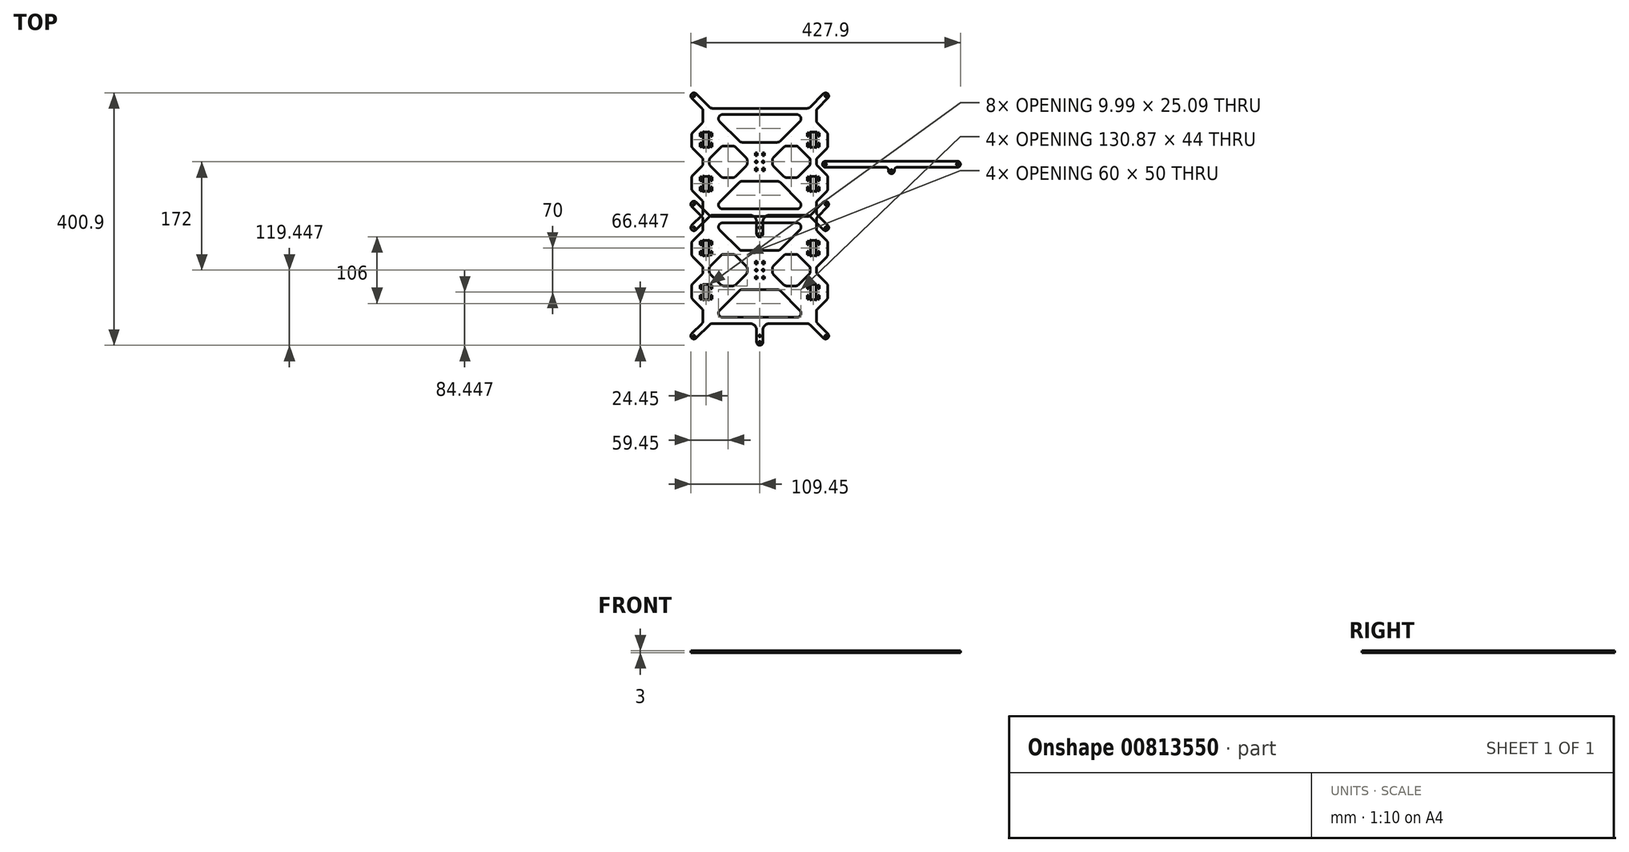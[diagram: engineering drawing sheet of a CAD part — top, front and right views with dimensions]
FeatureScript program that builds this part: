
annotation { "Feature Type Name" : "Feature", "Feature Type Description" : "" }
export const myFeature = defineFeature(function(context is Context, id is Id, definition is map)
    precondition{}
    {
        {
            var Q0;
            Q0=qCreatedBy(makeId("Top.planeOp"),FACE);
            var sketch = newSketch(context, id + "F0", { "sketchPlane" : qUnion([Q0])});
            skCircle(sketch, "E0", {"center": v(5.5, 8.85) * mm, "radius": 1.6 * mm});
            skCircle(sketch, "E1", {"center": v(-104.5, -95.65) * mm, "radius": 1.25 * mm});
            skCircle(sketch, "E2", {"center": v(-104.5, 113.35) * mm, "radius": 1.25 * mm});
            skCircle(sketch, "E3", {"center": v(0, -105.65) * mm, "radius": 1.6 * mm});
            skArc(sketch, "E4", {"start": v(-91.76, 70.09) * mm, "mid": v(-90.46, 72.04) * mm, "end": v(-90, 74.33) * mm});
            skLineSegment(sketch, "E5", {"start": v(-91.76, 70.09) * mm, "end": v(-106.24, 55.6) * mm});
            skArc(sketch, "E6", {"start": v(-106.24, 55.6) * mm, "mid": v(-107.54, 53.66) * mm, "end": v(-108, 51.36) * mm});
            skLineSegment(sketch, "E7", {"start": v(-108, 51.36) * mm, "end": v(-108, 34.33) * mm});
            skArc(sketch, "E8", {"start": v(-108, 34.33) * mm, "mid": v(-107.54, 32.04) * mm, "end": v(-106.24, 30.09) * mm});
            skLineSegment(sketch, "E9", {"start": v(-106.24, 30.09) * mm, "end": v(-91.76, 15.6) * mm});
            skArc(sketch, "E10", {"start": v(-90, 11.36) * mm, "mid": v(-90.46, 13.66) * mm, "end": v(-91.76, 15.6) * mm});
            skLineSegment(sketch, "E11", {"start": v(-90, 11.36) * mm, "end": v(-90, 6.33) * mm});
            skArc(sketch, "E12", {"start": v(-91.76, 2.09) * mm, "mid": v(-90.46, 4.04) * mm, "end": v(-90, 6.33) * mm});
            skLineSegment(sketch, "E13", {"start": v(-91.76, 2.09) * mm, "end": v(-106.24, -12.4) * mm});
            skArc(sketch, "E14", {"start": v(-106.24, -12.4) * mm, "mid": v(-107.54, -14.34) * mm, "end": v(-108, -16.64) * mm});
            skLineSegment(sketch, "E15", {"start": v(-108, -16.64) * mm, "end": v(-108, -33.67) * mm});
            skArc(sketch, "E16", {"start": v(-108, -33.67) * mm, "mid": v(-107.54, -35.96) * mm, "end": v(-106.24, -37.91) * mm});
            skLineSegment(sketch, "E17", {"start": v(-106.24, -37.91) * mm, "end": v(-91.76, -52.4) * mm});
            skArc(sketch, "E18", {"start": v(-90, -56.64) * mm, "mid": v(-90.46, -54.34) * mm, "end": v(-91.76, -52.4) * mm});
            skLineSegment(sketch, "E19", {"start": v(-90, -56.64) * mm, "end": v(-90, -71.67) * mm});
            skArc(sketch, "E20", {"start": v(-91.76, -75.91) * mm, "mid": v(-90.46, -73.96) * mm, "end": v(-90, -71.67) * mm});
            skLineSegment(sketch, "E21", {"start": v(-91.76, -75.91) * mm, "end": v(-108, -92.15) * mm});
            skArc(sketch, "E22", {"start": v(-108, -92.15) * mm, "mid": v(-108, -99.15) * mm, "end": v(-101, -99.15) * mm});
            skLineSegment(sketch, "E23", {"start": v(-101, -99.15) * mm, "end": v(-79.76, -77.91) * mm});
            skArc(sketch, "E24", {"start": v(-75.51, -76.15) * mm, "mid": v(-77.81, -76.6) * mm, "end": v(-79.76, -77.91) * mm});
            skLineSegment(sketch, "E25", {"start": v(-75.51, -76.15) * mm, "end": v(-14.95, -76.15) * mm});
            skArc(sketch, "E26", {"start": v(-4.95, -86.15) * mm, "mid": v(-7.88, -79.08) * mm, "end": v(-14.95, -76.15) * mm});
            skLineSegment(sketch, "E27", {"start": v(-4.95, -86.15) * mm, "end": v(-4.95, -105.65) * mm});
            skArc(sketch, "E28", {"start": v(-4.95, -105.65) * mm, "mid": v(0, -110.6) * mm, "end": v(4.95, -105.65) * mm});
            skLineSegment(sketch, "E29", {"start": v(4.95, -105.65) * mm, "end": v(4.95, -86.15) * mm});
            skArc(sketch, "E30", {"start": v(14.95, -76.15) * mm, "mid": v(7.88, -79.08) * mm, "end": v(4.95, -86.15) * mm});
            skLineSegment(sketch, "E31", {"start": v(14.95, -76.15) * mm, "end": v(75.51, -76.15) * mm});
            skArc(sketch, "E32", {"start": v(79.76, -77.91) * mm, "mid": v(77.81, -76.6) * mm, "end": v(75.51, -76.15) * mm});
            skLineSegment(sketch, "E33", {"start": v(79.76, -77.91) * mm, "end": v(101, -99.15) * mm});
            skArc(sketch, "E34", {"start": v(101, -99.15) * mm, "mid": v(108, -99.15) * mm, "end": v(108, -92.15) * mm});
            skLineSegment(sketch, "E35", {"start": v(108, -92.15) * mm, "end": v(91.76, -75.91) * mm});
            skArc(sketch, "E36", {"start": v(90, -71.67) * mm, "mid": v(90.46, -73.96) * mm, "end": v(91.76, -75.91) * mm});
            skLineSegment(sketch, "E37", {"start": v(90, -71.67) * mm, "end": v(90, -56.64) * mm});
            skArc(sketch, "E38", {"start": v(91.76, -52.4) * mm, "mid": v(90.46, -54.34) * mm, "end": v(90, -56.64) * mm});
            skLineSegment(sketch, "E39", {"start": v(91.76, -52.4) * mm, "end": v(106.24, -37.91) * mm});
            skArc(sketch, "E40", {"start": v(106.24, -37.91) * mm, "mid": v(107.54, -35.96) * mm, "end": v(108, -33.67) * mm});
            skLineSegment(sketch, "E41", {"start": v(108, -33.67) * mm, "end": v(108, -16.64) * mm});
            skArc(sketch, "E42", {"start": v(108, -16.64) * mm, "mid": v(107.54, -14.34) * mm, "end": v(106.24, -12.4) * mm});
            skLineSegment(sketch, "E43", {"start": v(106.24, -12.4) * mm, "end": v(91.76, 2.09) * mm});
            skArc(sketch, "E44", {"start": v(90, 6.33) * mm, "mid": v(90.46, 4.04) * mm, "end": v(91.76, 2.09) * mm});
            skLineSegment(sketch, "E45", {"start": v(90, 6.33) * mm, "end": v(90, 11.36) * mm});
            skArc(sketch, "E46", {"start": v(91.76, 15.6) * mm, "mid": v(90.46, 13.66) * mm, "end": v(90, 11.36) * mm});
            skLineSegment(sketch, "E47", {"start": v(91.76, 15.6) * mm, "end": v(106.24, 30.09) * mm});
            skArc(sketch, "E48", {"start": v(106.24, 30.09) * mm, "mid": v(107.54, 32.04) * mm, "end": v(108, 34.33) * mm});
            skLineSegment(sketch, "E49", {"start": v(108, 34.33) * mm, "end": v(108, 51.36) * mm});
            skArc(sketch, "E50", {"start": v(108, 51.36) * mm, "mid": v(107.54, 53.66) * mm, "end": v(106.24, 55.6) * mm});
            skLineSegment(sketch, "E51", {"start": v(106.24, 55.6) * mm, "end": v(91.76, 70.09) * mm});
            skArc(sketch, "E52", {"start": v(90, 74.33) * mm, "mid": v(90.46, 72.04) * mm, "end": v(91.76, 70.09) * mm});
            skLineSegment(sketch, "E53", {"start": v(90, 74.33) * mm, "end": v(90, 89.36) * mm});
            skArc(sketch, "E54", {"start": v(91.76, 93.6) * mm, "mid": v(90.46, 91.66) * mm, "end": v(90, 89.36) * mm});
            skLineSegment(sketch, "E55", {"start": v(91.76, 93.6) * mm, "end": v(108, 109.85) * mm});
            skArc(sketch, "E56", {"start": v(108, 109.85) * mm, "mid": v(108, 116.85) * mm, "end": v(101, 116.85) * mm});
            skLineSegment(sketch, "E57", {"start": v(101, 116.85) * mm, "end": v(79.76, 95.6) * mm});
            skArc(sketch, "E58", {"start": v(75.51, 93.85) * mm, "mid": v(77.81, 94.3) * mm, "end": v(79.76, 95.6) * mm});
            skLineSegment(sketch, "E59", {"start": v(75.51, 93.85) * mm, "end": v(-75.51, 93.85) * mm});
            skArc(sketch, "E60", {"start": v(-79.76, 95.6) * mm, "mid": v(-77.81, 94.3) * mm, "end": v(-75.51, 93.85) * mm});
            skLineSegment(sketch, "E61", {"start": v(-79.76, 95.6) * mm, "end": v(-101, 116.85) * mm});
            skArc(sketch, "E62", {"start": v(-101, 116.85) * mm, "mid": v(-108, 116.85) * mm, "end": v(-108, 109.85) * mm});
            skLineSegment(sketch, "E63", {"start": v(-108, 109.85) * mm, "end": v(-91.76, 93.6) * mm});
            skArc(sketch, "E64", {"start": v(-90, 89.36) * mm, "mid": v(-90.46, 91.66) * mm, "end": v(-91.76, 93.6) * mm});
            skLineSegment(sketch, "E65", {"start": v(-90, 89.36) * mm, "end": v(-90, 74.33) * mm});
            skLineSegment(sketch, "E66", {"start": v(89.5, -37.34) * mm, "end": v(89.5, -14.97) * mm});
            skArc(sketch, "E67", {"start": v(89.5, -37.34) * mm, "mid": v(89.57, -37.59) * mm, "end": v(89.75, -37.77) * mm});
            skArc(sketch, "E68", {"start": v(89.07, -38.45) * mm, "mid": v(89.85, -38.56) * mm, "end": v(89.75, -37.77) * mm});
            skArc(sketch, "E69", {"start": v(89.07, -38.45) * mm, "mid": v(88.88, -38.27) * mm, "end": v(88.63, -38.2) * mm});
            skLineSegment(sketch, "E70", {"start": v(81.37, -38.2) * mm, "end": v(88.63, -38.2) * mm});
            skArc(sketch, "E71", {"start": v(81.37, -38.2) * mm, "mid": v(81.12, -38.27) * mm, "end": v(80.93, -38.45) * mm});
            skArc(sketch, "E72", {"start": v(80.25, -37.77) * mm, "mid": v(80.15, -38.56) * mm, "end": v(80.93, -38.45) * mm});
            skArc(sketch, "E73", {"start": v(80.25, -37.77) * mm, "mid": v(80.43, -37.59) * mm, "end": v(80.5, -37.34) * mm});
            skLineSegment(sketch, "E74", {"start": v(80.5, -14.97) * mm, "end": v(80.5, -37.34) * mm});
            skArc(sketch, "E75", {"start": v(80.5, -14.97) * mm, "mid": v(80.43, -14.72) * mm, "end": v(80.25, -14.54) * mm});
            skArc(sketch, "E76", {"start": v(80.93, -13.85) * mm, "mid": v(80.15, -13.75) * mm, "end": v(80.25, -14.54) * mm});
            skArc(sketch, "E77", {"start": v(80.93, -13.85) * mm, "mid": v(81.12, -14.04) * mm, "end": v(81.37, -14.1) * mm});
            skLineSegment(sketch, "E78", {"start": v(88.63, -14.1) * mm, "end": v(81.37, -14.1) * mm});
            skArc(sketch, "E79", {"start": v(88.63, -14.1) * mm, "mid": v(88.88, -14.04) * mm, "end": v(89.07, -13.85) * mm});
            skArc(sketch, "E80", {"start": v(89.75, -14.54) * mm, "mid": v(89.85, -13.75) * mm, "end": v(89.07, -13.85) * mm});
            skArc(sketch, "E81", {"start": v(89.75, -14.54) * mm, "mid": v(89.57, -14.72) * mm, "end": v(89.5, -14.97) * mm});
            skLineSegment(sketch, "E82", {"start": v(32.73, 41.78) * mm, "end": v(63.53, 72.58) * mm});
            skArc(sketch, "E83", {"start": v(28.07, 39.85) * mm, "mid": v(30.6, 40.35) * mm, "end": v(32.73, 41.78) * mm});
            skLineSegment(sketch, "E84", {"start": v(-28.07, 39.85) * mm, "end": v(28.07, 39.85) * mm});
            skArc(sketch, "E85", {"start": v(-32.73, 41.78) * mm, "mid": v(-30.6, 40.35) * mm, "end": v(-28.07, 39.85) * mm});
            skLineSegment(sketch, "E86", {"start": v(-63.53, 72.58) * mm, "end": v(-32.73, 41.78) * mm});
            skArc(sketch, "E87", {"start": v(-58.87, 83.85) * mm, "mid": v(-64.96, 79.77) * mm, "end": v(-63.53, 72.58) * mm});
            skLineSegment(sketch, "E88", {"start": v(58.87, 83.85) * mm, "end": v(-58.87, 83.85) * mm});
            skArc(sketch, "E89", {"start": v(63.53, 72.58) * mm, "mid": v(64.96, 79.77) * mm, "end": v(58.87, 83.85) * mm});
            skLineSegment(sketch, "E90", {"start": v(21.76, 2.09) * mm, "end": v(38.24, -14.4) * mm});
            skArc(sketch, "E91", {"start": v(20, 6.33) * mm, "mid": v(20.46, 4.04) * mm, "end": v(21.76, 2.09) * mm});
            skLineSegment(sketch, "E92", {"start": v(20, 11.36) * mm, "end": v(20, 6.33) * mm});
            skArc(sketch, "E93", {"start": v(21.76, 15.6) * mm, "mid": v(20.46, 13.66) * mm, "end": v(20, 11.36) * mm});
            skLineSegment(sketch, "E94", {"start": v(38.24, 32.09) * mm, "end": v(21.76, 15.6) * mm});
            skArc(sketch, "E95", {"start": v(42.49, 33.85) * mm, "mid": v(40.19, 33.4) * mm, "end": v(38.24, 32.09) * mm});
            skLineSegment(sketch, "E96", {"start": v(57.51, 33.85) * mm, "end": v(42.49, 33.85) * mm});
            skArc(sketch, "E97", {"start": v(61.76, 32.09) * mm, "mid": v(59.81, 33.4) * mm, "end": v(57.51, 33.85) * mm});
            skLineSegment(sketch, "E98", {"start": v(78.24, 15.6) * mm, "end": v(61.76, 32.09) * mm});
            skArc(sketch, "E99", {"start": v(80, 11.36) * mm, "mid": v(79.54, 13.66) * mm, "end": v(78.24, 15.6) * mm});
            skLineSegment(sketch, "E100", {"start": v(80, 6.33) * mm, "end": v(80, 11.36) * mm});
            skArc(sketch, "E101", {"start": v(78.24, 2.09) * mm, "mid": v(79.54, 4.04) * mm, "end": v(80, 6.33) * mm});
            skLineSegment(sketch, "E102", {"start": v(61.76, -14.4) * mm, "end": v(78.24, 2.09) * mm});
            skArc(sketch, "E103", {"start": v(57.51, -16.15) * mm, "mid": v(59.81, -15.7) * mm, "end": v(61.76, -14.4) * mm});
            skLineSegment(sketch, "E104", {"start": v(42.49, -16.15) * mm, "end": v(57.51, -16.15) * mm});
            skArc(sketch, "E105", {"start": v(38.24, -14.4) * mm, "mid": v(40.19, -15.7) * mm, "end": v(42.49, -16.15) * mm});
            skLineSegment(sketch, "E106", {"start": v(63.53, -54.89) * mm, "end": v(32.73, -24.09) * mm});
            skArc(sketch, "E107", {"start": v(58.87, -66.15) * mm, "mid": v(64.96, -62.08) * mm, "end": v(63.53, -54.89) * mm});
            skLineSegment(sketch, "E108", {"start": v(-58.87, -66.15) * mm, "end": v(58.87, -66.15) * mm});
            skArc(sketch, "E109", {"start": v(-63.53, -54.89) * mm, "mid": v(-64.96, -62.08) * mm, "end": v(-58.87, -66.15) * mm});
            skLineSegment(sketch, "E110", {"start": v(-32.73, -24.09) * mm, "end": v(-63.53, -54.89) * mm});
            skArc(sketch, "E111", {"start": v(-28.07, -22.15) * mm, "mid": v(-30.6, -22.66) * mm, "end": v(-32.73, -24.09) * mm});
            skLineSegment(sketch, "E112", {"start": v(28.07, -22.15) * mm, "end": v(-28.07, -22.15) * mm});
            skArc(sketch, "E113", {"start": v(32.73, -24.09) * mm, "mid": v(30.6, -22.66) * mm, "end": v(28.07, -22.15) * mm});
            skLineSegment(sketch, "E114", {"start": v(-61.76, 32.09) * mm, "end": v(-78.24, 15.6) * mm});
            skArc(sketch, "E115", {"start": v(-57.51, 33.85) * mm, "mid": v(-59.81, 33.4) * mm, "end": v(-61.76, 32.09) * mm});
            skLineSegment(sketch, "E116", {"start": v(-42.49, 33.85) * mm, "end": v(-57.51, 33.85) * mm});
            skArc(sketch, "E117", {"start": v(-38.24, 32.09) * mm, "mid": v(-40.19, 33.4) * mm, "end": v(-42.49, 33.85) * mm});
            skLineSegment(sketch, "E118", {"start": v(-21.76, 15.6) * mm, "end": v(-38.24, 32.09) * mm});
            skArc(sketch, "E119", {"start": v(-20, 11.36) * mm, "mid": v(-20.46, 13.66) * mm, "end": v(-21.76, 15.6) * mm});
            skLineSegment(sketch, "E120", {"start": v(-20, 6.33) * mm, "end": v(-20, 11.36) * mm});
            skArc(sketch, "E121", {"start": v(-21.76, 2.09) * mm, "mid": v(-20.46, 4.04) * mm, "end": v(-20, 6.33) * mm});
            skLineSegment(sketch, "E122", {"start": v(-38.24, -14.4) * mm, "end": v(-21.76, 2.09) * mm});
            skArc(sketch, "E123", {"start": v(-42.49, -16.15) * mm, "mid": v(-40.19, -15.7) * mm, "end": v(-38.24, -14.4) * mm});
            skLineSegment(sketch, "E124", {"start": v(-57.51, -16.15) * mm, "end": v(-42.49, -16.15) * mm});
            skArc(sketch, "E125", {"start": v(-61.76, -14.4) * mm, "mid": v(-59.81, -15.7) * mm, "end": v(-57.51, -16.15) * mm});
            skLineSegment(sketch, "E126", {"start": v(-78.24, 2.09) * mm, "end": v(-61.76, -14.4) * mm});
            skArc(sketch, "E127", {"start": v(-80, 6.33) * mm, "mid": v(-79.54, 4.04) * mm, "end": v(-78.24, 2.09) * mm});
            skLineSegment(sketch, "E128", {"start": v(-80, 11.36) * mm, "end": v(-80, 6.33) * mm});
            skArc(sketch, "E129", {"start": v(-78.24, 15.6) * mm, "mid": v(-79.54, 13.66) * mm, "end": v(-80, 11.36) * mm});
            skLineSegment(sketch, "E130", {"start": v(-88.63, 31.8) * mm, "end": v(-81.37, 31.8) * mm});
            skArc(sketch, "E131", {"start": v(-88.63, 31.8) * mm, "mid": v(-88.88, 31.73) * mm, "end": v(-89.07, 31.55) * mm});
            skArc(sketch, "E132", {"start": v(-89.75, 32.23) * mm, "mid": v(-89.85, 31.44) * mm, "end": v(-89.07, 31.55) * mm});
            skArc(sketch, "E133", {"start": v(-89.75, 32.23) * mm, "mid": v(-89.57, 32.41) * mm, "end": v(-89.5, 32.66) * mm});
            skLineSegment(sketch, "E134", {"start": v(-89.5, 55.03) * mm, "end": v(-89.5, 32.66) * mm});
            skArc(sketch, "E135", {"start": v(-89.5, 55.03) * mm, "mid": v(-89.57, 55.28) * mm, "end": v(-89.75, 55.46) * mm});
            skArc(sketch, "E136", {"start": v(-89.07, 56.15) * mm, "mid": v(-89.85, 56.25) * mm, "end": v(-89.75, 55.46) * mm});
            skArc(sketch, "E137", {"start": v(-89.07, 56.15) * mm, "mid": v(-88.88, 55.96) * mm, "end": v(-88.63, 55.9) * mm});
            skLineSegment(sketch, "E138", {"start": v(-81.37, 55.9) * mm, "end": v(-88.63, 55.9) * mm});
            skArc(sketch, "E139", {"start": v(-81.37, 55.9) * mm, "mid": v(-81.12, 55.96) * mm, "end": v(-80.93, 56.15) * mm});
            skArc(sketch, "E140", {"start": v(-80.25, 55.46) * mm, "mid": v(-80.15, 56.25) * mm, "end": v(-80.93, 56.15) * mm});
            skArc(sketch, "E141", {"start": v(-80.25, 55.46) * mm, "mid": v(-80.43, 55.28) * mm, "end": v(-80.5, 55.03) * mm});
            skLineSegment(sketch, "E142", {"start": v(-80.5, 32.66) * mm, "end": v(-80.5, 55.03) * mm});
            skArc(sketch, "E143", {"start": v(-80.5, 32.66) * mm, "mid": v(-80.43, 32.41) * mm, "end": v(-80.25, 32.23) * mm});
            skArc(sketch, "E144", {"start": v(-80.93, 31.55) * mm, "mid": v(-80.15, 31.44) * mm, "end": v(-80.25, 32.23) * mm});
            skArc(sketch, "E145", {"start": v(-80.93, 31.55) * mm, "mid": v(-81.12, 31.73) * mm, "end": v(-81.37, 31.8) * mm});
            skLineSegment(sketch, "E146", {"start": v(-88.63, -38.2) * mm, "end": v(-81.37, -38.2) * mm});
            skArc(sketch, "E147", {"start": v(-88.63, -38.2) * mm, "mid": v(-88.88, -38.27) * mm, "end": v(-89.07, -38.45) * mm});
            skArc(sketch, "E148", {"start": v(-89.75, -37.77) * mm, "mid": v(-89.85, -38.56) * mm, "end": v(-89.07, -38.45) * mm});
            skArc(sketch, "E149", {"start": v(-89.75, -37.77) * mm, "mid": v(-89.57, -37.59) * mm, "end": v(-89.5, -37.34) * mm});
            skLineSegment(sketch, "E150", {"start": v(-89.5, -14.97) * mm, "end": v(-89.5, -37.34) * mm});
            skArc(sketch, "E151", {"start": v(-89.5, -14.97) * mm, "mid": v(-89.57, -14.72) * mm, "end": v(-89.75, -14.54) * mm});
            skArc(sketch, "E152", {"start": v(-89.07, -13.85) * mm, "mid": v(-89.85, -13.75) * mm, "end": v(-89.75, -14.54) * mm});
            skArc(sketch, "E153", {"start": v(-89.07, -13.85) * mm, "mid": v(-88.88, -14.04) * mm, "end": v(-88.63, -14.1) * mm});
            skLineSegment(sketch, "E154", {"start": v(-81.37, -14.1) * mm, "end": v(-88.63, -14.1) * mm});
            skArc(sketch, "E155", {"start": v(-81.37, -14.1) * mm, "mid": v(-81.12, -14.04) * mm, "end": v(-80.93, -13.85) * mm});
            skArc(sketch, "E156", {"start": v(-80.25, -14.54) * mm, "mid": v(-80.15, -13.75) * mm, "end": v(-80.93, -13.85) * mm});
            skArc(sketch, "E157", {"start": v(-80.25, -14.54) * mm, "mid": v(-80.43, -14.72) * mm, "end": v(-80.5, -14.97) * mm});
            skLineSegment(sketch, "E158", {"start": v(-80.5, -37.34) * mm, "end": v(-80.5, -14.97) * mm});
            skArc(sketch, "E159", {"start": v(-80.5, -37.34) * mm, "mid": v(-80.43, -37.59) * mm, "end": v(-80.25, -37.77) * mm});
            skArc(sketch, "E160", {"start": v(-80.93, -38.45) * mm, "mid": v(-80.15, -38.56) * mm, "end": v(-80.25, -37.77) * mm});
            skArc(sketch, "E161", {"start": v(-80.93, -38.45) * mm, "mid": v(-81.12, -38.27) * mm, "end": v(-81.37, -38.2) * mm});
            skLineSegment(sketch, "E162", {"start": v(89.5, 32.66) * mm, "end": v(89.5, 55.03) * mm});
            skArc(sketch, "E163", {"start": v(89.5, 32.66) * mm, "mid": v(89.57, 32.41) * mm, "end": v(89.75, 32.23) * mm});
            skArc(sketch, "E164", {"start": v(89.07, 31.55) * mm, "mid": v(89.85, 31.44) * mm, "end": v(89.75, 32.23) * mm});
            skArc(sketch, "E165", {"start": v(89.07, 31.55) * mm, "mid": v(88.88, 31.73) * mm, "end": v(88.63, 31.8) * mm});
            skLineSegment(sketch, "E166", {"start": v(81.37, 31.8) * mm, "end": v(88.63, 31.8) * mm});
            skArc(sketch, "E167", {"start": v(81.37, 31.8) * mm, "mid": v(81.12, 31.73) * mm, "end": v(80.93, 31.55) * mm});
            skArc(sketch, "E168", {"start": v(80.25, 32.23) * mm, "mid": v(80.15, 31.44) * mm, "end": v(80.93, 31.55) * mm});
            skArc(sketch, "E169", {"start": v(80.25, 32.23) * mm, "mid": v(80.43, 32.41) * mm, "end": v(80.5, 32.66) * mm});
            skLineSegment(sketch, "E170", {"start": v(80.5, 55.03) * mm, "end": v(80.5, 32.66) * mm});
            skArc(sketch, "E171", {"start": v(80.5, 55.03) * mm, "mid": v(80.43, 55.28) * mm, "end": v(80.25, 55.46) * mm});
            skArc(sketch, "E172", {"start": v(80.93, 56.15) * mm, "mid": v(80.15, 56.25) * mm, "end": v(80.25, 55.46) * mm});
            skArc(sketch, "E173", {"start": v(80.93, 56.15) * mm, "mid": v(81.12, 55.96) * mm, "end": v(81.37, 55.9) * mm});
            skLineSegment(sketch, "E174", {"start": v(88.63, 55.9) * mm, "end": v(81.37, 55.9) * mm});
            skArc(sketch, "E175", {"start": v(88.63, 55.9) * mm, "mid": v(88.88, 55.96) * mm, "end": v(89.07, 56.15) * mm});
            skArc(sketch, "E176", {"start": v(89.75, 55.46) * mm, "mid": v(89.85, 56.25) * mm, "end": v(89.07, 56.15) * mm});
            skArc(sketch, "E177", {"start": v(89.75, 55.46) * mm, "mid": v(89.57, 55.28) * mm, "end": v(89.5, 55.03) * mm});
            skCircle(sketch, "E178", {"center": v(0, -95.65) * mm, "radius": 1.6 * mm});
            skCircle(sketch, "E179", {"center": v(104.5, 113.35) * mm, "radius": 1.25 * mm});
            skCircle(sketch, "E180", {"center": v(104.5, -95.65) * mm, "radius": 1.25 * mm});
            skCircle(sketch, "E181", {"center": v(-5.5, 8.85) * mm, "radius": 1.6 * mm});
            skLineSegment(sketch, "E182", {"start": v(7.2, -1.05) * mm, "end": v(4, -1.05) * mm});
            skLineSegment(sketch, "E183", {"start": v(7.2, -5.25) * mm, "end": v(7.2, -1.05) * mm});
            skLineSegment(sketch, "E184", {"start": v(4, -5.25) * mm, "end": v(7.2, -5.25) * mm});
            skLineSegment(sketch, "E185", {"start": v(4, -1.05) * mm, "end": v(4, -5.25) * mm});
            skLineSegment(sketch, "E186", {"start": v(7.2, 22.95) * mm, "end": v(4, 22.95) * mm});
            skLineSegment(sketch, "E187", {"start": v(7.2, 18.75) * mm, "end": v(7.2, 22.95) * mm});
            skLineSegment(sketch, "E188", {"start": v(4, 18.75) * mm, "end": v(7.2, 18.75) * mm});
            skLineSegment(sketch, "E189", {"start": v(4, 22.95) * mm, "end": v(4, 18.75) * mm});
            skLineSegment(sketch, "E190", {"start": v(-7.2, -5.25) * mm, "end": v(-4, -5.25) * mm});
            skLineSegment(sketch, "E191", {"start": v(-7.2, -1.05) * mm, "end": v(-7.2, -5.25) * mm});
            skLineSegment(sketch, "E192", {"start": v(-4, -1.05) * mm, "end": v(-7.2, -1.05) * mm});
            skLineSegment(sketch, "E193", {"start": v(-4, -5.25) * mm, "end": v(-4, -1.05) * mm});
            skLineSegment(sketch, "E194", {"start": v(-7.2, 18.75) * mm, "end": v(-4, 18.75) * mm});
            skLineSegment(sketch, "E195", {"start": v(-7.2, 22.95) * mm, "end": v(-7.2, 18.75) * mm});
            skLineSegment(sketch, "E196", {"start": v(-4, 22.95) * mm, "end": v(-7.2, 22.95) * mm});
            skLineSegment(sketch, "E197", {"start": v(-4, 18.75) * mm, "end": v(-4, 22.95) * mm});
            skLineSegment(sketch, "E198", {"start": v(-75.5, 38.85) * mm, "end": v(-77.5, 38.85) * mm});
            skLineSegment(sketch, "E199", {"start": v(-75.5, 32.85) * mm, "end": v(-75.5, 38.85) * mm});
            skLineSegment(sketch, "E200", {"start": v(-77.5, 32.85) * mm, "end": v(-75.5, 32.85) * mm});
            skLineSegment(sketch, "E201", {"start": v(-77.5, 38.85) * mm, "end": v(-77.5, 32.85) * mm});
            skLineSegment(sketch, "E202", {"start": v(-92.5, 38.85) * mm, "end": v(-94.5, 38.85) * mm});
            skLineSegment(sketch, "E203", {"start": v(-92.5, 32.85) * mm, "end": v(-92.5, 38.85) * mm});
            skLineSegment(sketch, "E204", {"start": v(-94.5, 32.85) * mm, "end": v(-92.5, 32.85) * mm});
            skLineSegment(sketch, "E205", {"start": v(-94.5, 38.85) * mm, "end": v(-94.5, 32.85) * mm});
            skLineSegment(sketch, "E206", {"start": v(-77.5, 48.85) * mm, "end": v(-75.5, 48.85) * mm});
            skLineSegment(sketch, "E207", {"start": v(-77.5, 54.85) * mm, "end": v(-77.5, 48.85) * mm});
            skLineSegment(sketch, "E208", {"start": v(-75.5, 54.85) * mm, "end": v(-77.5, 54.85) * mm});
            skLineSegment(sketch, "E209", {"start": v(-75.5, 48.85) * mm, "end": v(-75.5, 54.85) * mm});
            skLineSegment(sketch, "E210", {"start": v(-94.5, 48.85) * mm, "end": v(-92.5, 48.85) * mm});
            skLineSegment(sketch, "E211", {"start": v(-94.5, 54.85) * mm, "end": v(-94.5, 48.85) * mm});
            skLineSegment(sketch, "E212", {"start": v(-92.5, 54.85) * mm, "end": v(-94.5, 54.85) * mm});
            skLineSegment(sketch, "E213", {"start": v(-92.5, 48.85) * mm, "end": v(-92.5, 54.85) * mm});
            skLineSegment(sketch, "E214", {"start": v(94.5, 38.85) * mm, "end": v(92.5, 38.85) * mm});
            skLineSegment(sketch, "E215", {"start": v(94.5, 32.85) * mm, "end": v(94.5, 38.85) * mm});
            skLineSegment(sketch, "E216", {"start": v(92.5, 32.85) * mm, "end": v(94.5, 32.85) * mm});
            skLineSegment(sketch, "E217", {"start": v(92.5, 38.85) * mm, "end": v(92.5, 32.85) * mm});
            skLineSegment(sketch, "E218", {"start": v(77.5, 38.85) * mm, "end": v(75.5, 38.85) * mm});
            skLineSegment(sketch, "E219", {"start": v(77.5, 32.85) * mm, "end": v(77.5, 38.85) * mm});
            skLineSegment(sketch, "E220", {"start": v(75.5, 32.85) * mm, "end": v(77.5, 32.85) * mm});
            skLineSegment(sketch, "E221", {"start": v(75.5, 38.85) * mm, "end": v(75.5, 32.85) * mm});
            skLineSegment(sketch, "E222", {"start": v(92.5, 48.85) * mm, "end": v(94.5, 48.85) * mm});
            skLineSegment(sketch, "E223", {"start": v(92.5, 54.85) * mm, "end": v(92.5, 48.85) * mm});
            skLineSegment(sketch, "E224", {"start": v(94.5, 54.85) * mm, "end": v(92.5, 54.85) * mm});
            skLineSegment(sketch, "E225", {"start": v(94.5, 48.85) * mm, "end": v(94.5, 54.85) * mm});
            skLineSegment(sketch, "E226", {"start": v(75.5, 48.85) * mm, "end": v(77.5, 48.85) * mm});
            skLineSegment(sketch, "E227", {"start": v(75.5, 54.85) * mm, "end": v(75.5, 48.85) * mm});
            skLineSegment(sketch, "E228", {"start": v(77.5, 54.85) * mm, "end": v(75.5, 54.85) * mm});
            skLineSegment(sketch, "E229", {"start": v(77.5, 48.85) * mm, "end": v(77.5, 54.85) * mm});
            skLineSegment(sketch, "E230", {"start": v(94.5, -31.15) * mm, "end": v(92.5, -31.15) * mm});
            skLineSegment(sketch, "E231", {"start": v(94.5, -37.15) * mm, "end": v(94.5, -31.15) * mm});
            skLineSegment(sketch, "E232", {"start": v(92.5, -37.15) * mm, "end": v(94.5, -37.15) * mm});
            skLineSegment(sketch, "E233", {"start": v(92.5, -31.15) * mm, "end": v(92.5, -37.15) * mm});
            skLineSegment(sketch, "E234", {"start": v(77.5, -31.15) * mm, "end": v(75.5, -31.15) * mm});
            skLineSegment(sketch, "E235", {"start": v(77.5, -37.15) * mm, "end": v(77.5, -31.15) * mm});
            skLineSegment(sketch, "E236", {"start": v(75.5, -37.15) * mm, "end": v(77.5, -37.15) * mm});
            skLineSegment(sketch, "E237", {"start": v(75.5, -31.15) * mm, "end": v(75.5, -37.15) * mm});
            skLineSegment(sketch, "E238", {"start": v(92.5, -21.15) * mm, "end": v(94.5, -21.15) * mm});
            skLineSegment(sketch, "E239", {"start": v(92.5, -15.15) * mm, "end": v(92.5, -21.15) * mm});
            skLineSegment(sketch, "E240", {"start": v(94.5, -15.15) * mm, "end": v(92.5, -15.15) * mm});
            skLineSegment(sketch, "E241", {"start": v(94.5, -21.15) * mm, "end": v(94.5, -15.15) * mm});
            skLineSegment(sketch, "E242", {"start": v(75.5, -21.15) * mm, "end": v(77.5, -21.15) * mm});
            skLineSegment(sketch, "E243", {"start": v(75.5, -15.15) * mm, "end": v(75.5, -21.15) * mm});
            skLineSegment(sketch, "E244", {"start": v(77.5, -15.15) * mm, "end": v(75.5, -15.15) * mm});
            skLineSegment(sketch, "E245", {"start": v(77.5, -21.15) * mm, "end": v(77.5, -15.15) * mm});
            skLineSegment(sketch, "E246", {"start": v(-75.5, -31.15) * mm, "end": v(-77.5, -31.15) * mm});
            skLineSegment(sketch, "E247", {"start": v(-75.5, -37.15) * mm, "end": v(-75.5, -31.15) * mm});
            skLineSegment(sketch, "E248", {"start": v(-77.5, -37.15) * mm, "end": v(-75.5, -37.15) * mm});
            skLineSegment(sketch, "E249", {"start": v(-77.5, -31.15) * mm, "end": v(-77.5, -37.15) * mm});
            skLineSegment(sketch, "E250", {"start": v(-92.5, -31.15) * mm, "end": v(-94.5, -31.15) * mm});
            skLineSegment(sketch, "E251", {"start": v(-92.5, -37.15) * mm, "end": v(-92.5, -31.15) * mm});
            skLineSegment(sketch, "E252", {"start": v(-94.5, -37.15) * mm, "end": v(-92.5, -37.15) * mm});
            skLineSegment(sketch, "E253", {"start": v(-94.5, -31.15) * mm, "end": v(-94.5, -37.15) * mm});
            skLineSegment(sketch, "E254", {"start": v(-77.5, -21.15) * mm, "end": v(-75.5, -21.15) * mm});
            skLineSegment(sketch, "E255", {"start": v(-77.5, -15.15) * mm, "end": v(-77.5, -21.15) * mm});
            skLineSegment(sketch, "E256", {"start": v(-75.5, -15.15) * mm, "end": v(-77.5, -15.15) * mm});
            skLineSegment(sketch, "E257", {"start": v(-75.5, -21.15) * mm, "end": v(-75.5, -15.15) * mm});
            skLineSegment(sketch, "E258", {"start": v(-94.5, -21.15) * mm, "end": v(-92.5, -21.15) * mm});
            skLineSegment(sketch, "E259", {"start": v(-94.5, -15.15) * mm, "end": v(-94.5, -21.15) * mm});
            skLineSegment(sketch, "E260", {"start": v(-92.5, -15.15) * mm, "end": v(-94.5, -15.15) * mm});
            skLineSegment(sketch, "E261", {"start": v(-92.5, -21.15) * mm, "end": v(-92.5, -15.15) * mm});
            skSolve(sketch);
        }
        {
            var Q0;
            Q0=qSketchRegion(id+"F0",true);
            extrude(context, id + "F1", {"entities" : qUnion([Q0]), "depth" : 3 * mm, "offsetDistance" : 25 * mm});
        }
        {
            var Q0;
            Q0=qCreatedBy(makeId("Top.planeOp"),FACE);
            var sketch = newSketch(context, id + "F2", { "sketchPlane" : qUnion([Q0])});
            skArc(sketch, "E262", {"start": v(104.5, 0.05) * mm, "mid": v(109.45, 5) * mm, "end": v(104.5, 9.95) * mm});
            skArc(sketch, "E263", {"start": v(-104.5, 9.95) * mm, "mid": v(-109.45, 5) * mm, "end": v(-104.5, 0.05) * mm});
            skCircle(sketch, "E264", {"center": v(-104.5, 5) * mm, "radius": 1.6 * mm});
            skCircle(sketch, "E265", {"center": v(104.5, 5) * mm, "radius": 1.6 * mm});
            skArc(sketch, "E266", {"start": v(-4.95, -5) * mm, "mid": v(0, -9.95) * mm, "end": v(4.95, -5) * mm});
            skCircle(sketch, "E267", {"center": v(0, -5) * mm, "radius": 1.6 * mm});
            skLineSegment(sketch, "E268", {"start": v(-8.95, 0.05) * mm, "end": v(-104.5, 0.05) * mm});
            skLineSegment(sketch, "E269", {"start": v(-4.95, -5) * mm, "end": v(-4.95, -3.95) * mm});
            skLineSegment(sketch, "E270", {"start": v(4.95, -3.95) * mm, "end": v(4.95, -5) * mm});
            skLineSegment(sketch, "E271", {"start": v(104.5, 0.05) * mm, "end": v(8.95, 0.05) * mm});
            skLineSegment(sketch, "E272", {"start": v(-104.5, 9.95) * mm, "end": v(104.5, 9.95) * mm});
            skArc(sketch, "E273", {"start": v(8.95, 0.05) * mm, "mid": v(6.12, -1.12) * mm, "end": v(4.95, -3.95) * mm});
            skArc(sketch, "E274", {"start": v(-4.95, -3.95) * mm, "mid": v(-6.12, -1.12) * mm, "end": v(-8.95, 0.05) * mm});
            skSolve(sketch);
        }
        {
            var Q0;
            Q0=qSketchRegion(id+"F2",true);
            extrude(context, id + "F3", {"entities" : qUnion([Q0]), "depth" : 3 * mm, "offsetDistance" : 25 * mm});
        }
        {
            var Q0;
            Q0=makeQuery(id+"F3.opExtrude","SWEPT_BODY",BODY,{"disambiguationData":[OSD([sQuery(id+"F2.wireOp",EDGE,"E262"),sQuery(id+"F2.wireOp",EDGE,"E263"),sQuery(id+"F2.wireOp",EDGE,"E264"),sQuery(id+"F2.wireOp",EDGE,"E265"),sQuery(id+"F2.wireOp",EDGE,"E266"),sQuery(id+"F2.wireOp",EDGE,"E267"),sQuery(id+"F2.wireOp",EDGE,"E268"),sQuery(id+"F2.wireOp",EDGE,"E269"),sQuery(id+"F2.wireOp",EDGE,"E270"),sQuery(id+"F2.wireOp",EDGE,"E271"),sQuery(id+"F2.wireOp",EDGE,"E272"),sQuery(id+"F2.wireOp",EDGE,"E273"),sQuery(id+"F2.wireOp",EDGE,"E274")])]});
            var Q1;
            Q1=makeQuery(id+"F3.opExtrude","CAP_EDGE",EDGE,{"disambiguationData":[OSD([sQuery(id+"F2.wireOp",EDGE,"E272")])],"isStart":false});
            transform(context, id + "F4", {"entities" : qUnion([Q0]), "transformType" : TransformType.TRANSLATION_ENTITY, "oppositeDirectionEntity" : false, "transformLine" : qUnion([Q1]), "makeCopy" : false});
        }
        {
            var Q0;
            Q0=makeQuery(id+"F1.opExtrude","SWEPT_BODY",BODY,{"disambiguationData":[OSD([sQuery(id+"F0.wireOp",EDGE,"E0"),sQuery(id+"F0.wireOp",EDGE,"E1"),sQuery(id+"F0.wireOp",EDGE,"E2"),sQuery(id+"F0.wireOp",EDGE,"E3"),sQuery(id+"F0.wireOp",EDGE,"E4"),sQuery(id+"F0.wireOp",EDGE,"E5"),sQuery(id+"F0.wireOp",EDGE,"E6"),sQuery(id+"F0.wireOp",EDGE,"E7"),sQuery(id+"F0.wireOp",EDGE,"E8"),sQuery(id+"F0.wireOp",EDGE,"E9"),sQuery(id+"F0.wireOp",EDGE,"E10"),sQuery(id+"F0.wireOp",EDGE,"E11"),sQuery(id+"F0.wireOp",EDGE,"E12"),sQuery(id+"F0.wireOp",EDGE,"E13"),sQuery(id+"F0.wireOp",EDGE,"E14"),sQuery(id+"F0.wireOp",EDGE,"E15"),sQuery(id+"F0.wireOp",EDGE,"E16"),sQuery(id+"F0.wireOp",EDGE,"E17"),sQuery(id+"F0.wireOp",EDGE,"E18"),sQuery(id+"F0.wireOp",EDGE,"E19"),sQuery(id+"F0.wireOp",EDGE,"E20"),sQuery(id+"F0.wireOp",EDGE,"E21"),sQuery(id+"F0.wireOp",EDGE,"E22"),sQuery(id+"F0.wireOp",EDGE,"E23"),sQuery(id+"F0.wireOp",EDGE,"E24"),sQuery(id+"F0.wireOp",EDGE,"E25"),sQuery(id+"F0.wireOp",EDGE,"E26"),sQuery(id+"F0.wireOp",EDGE,"E27"),sQuery(id+"F0.wireOp",EDGE,"E28"),sQuery(id+"F0.wireOp",EDGE,"E29"),sQuery(id+"F0.wireOp",EDGE,"E30"),sQuery(id+"F0.wireOp",EDGE,"E31"),sQuery(id+"F0.wireOp",EDGE,"E32"),sQuery(id+"F0.wireOp",EDGE,"E33"),sQuery(id+"F0.wireOp",EDGE,"E34"),sQuery(id+"F0.wireOp",EDGE,"E35"),sQuery(id+"F0.wireOp",EDGE,"E36"),sQuery(id+"F0.wireOp",EDGE,"E37"),sQuery(id+"F0.wireOp",EDGE,"E38"),sQuery(id+"F0.wireOp",EDGE,"E39"),sQuery(id+"F0.wireOp",EDGE,"E40"),sQuery(id+"F0.wireOp",EDGE,"E41"),sQuery(id+"F0.wireOp",EDGE,"E42"),sQuery(id+"F0.wireOp",EDGE,"E43"),sQuery(id+"F0.wireOp",EDGE,"E44"),sQuery(id+"F0.wireOp",EDGE,"E45"),sQuery(id+"F0.wireOp",EDGE,"E46"),sQuery(id+"F0.wireOp",EDGE,"E47"),sQuery(id+"F0.wireOp",EDGE,"E48"),sQuery(id+"F0.wireOp",EDGE,"E49"),sQuery(id+"F0.wireOp",EDGE,"E50"),sQuery(id+"F0.wireOp",EDGE,"E51"),sQuery(id+"F0.wireOp",EDGE,"E52"),sQuery(id+"F0.wireOp",EDGE,"E53"),sQuery(id+"F0.wireOp",EDGE,"E54"),sQuery(id+"F0.wireOp",EDGE,"E55"),sQuery(id+"F0.wireOp",EDGE,"E56"),sQuery(id+"F0.wireOp",EDGE,"E57"),sQuery(id+"F0.wireOp",EDGE,"E58"),sQuery(id+"F0.wireOp",EDGE,"E59"),sQuery(id+"F0.wireOp",EDGE,"E60"),sQuery(id+"F0.wireOp",EDGE,"E61"),sQuery(id+"F0.wireOp",EDGE,"E62"),sQuery(id+"F0.wireOp",EDGE,"E63"),sQuery(id+"F0.wireOp",EDGE,"E64"),sQuery(id+"F0.wireOp",EDGE,"E65"),sQuery(id+"F0.wireOp",EDGE,"E66"),sQuery(id+"F0.wireOp",EDGE,"E67"),sQuery(id+"F0.wireOp",EDGE,"E68"),sQuery(id+"F0.wireOp",EDGE,"E69"),sQuery(id+"F0.wireOp",EDGE,"E70"),sQuery(id+"F0.wireOp",EDGE,"E71"),sQuery(id+"F0.wireOp",EDGE,"E72"),sQuery(id+"F0.wireOp",EDGE,"E73"),sQuery(id+"F0.wireOp",EDGE,"E74"),sQuery(id+"F0.wireOp",EDGE,"E75"),sQuery(id+"F0.wireOp",EDGE,"E76"),sQuery(id+"F0.wireOp",EDGE,"E77"),sQuery(id+"F0.wireOp",EDGE,"E78"),sQuery(id+"F0.wireOp",EDGE,"E79"),sQuery(id+"F0.wireOp",EDGE,"E80"),sQuery(id+"F0.wireOp",EDGE,"E81"),sQuery(id+"F0.wireOp",EDGE,"E82"),sQuery(id+"F0.wireOp",EDGE,"E83"),sQuery(id+"F0.wireOp",EDGE,"E84"),sQuery(id+"F0.wireOp",EDGE,"E85"),sQuery(id+"F0.wireOp",EDGE,"E86"),sQuery(id+"F0.wireOp",EDGE,"E87"),sQuery(id+"F0.wireOp",EDGE,"E88"),sQuery(id+"F0.wireOp",EDGE,"E89"),sQuery(id+"F0.wireOp",EDGE,"E90"),sQuery(id+"F0.wireOp",EDGE,"E91"),sQuery(id+"F0.wireOp",EDGE,"E92"),sQuery(id+"F0.wireOp",EDGE,"E93"),sQuery(id+"F0.wireOp",EDGE,"E94"),sQuery(id+"F0.wireOp",EDGE,"E95"),sQuery(id+"F0.wireOp",EDGE,"E96"),sQuery(id+"F0.wireOp",EDGE,"E97"),sQuery(id+"F0.wireOp",EDGE,"E98"),sQuery(id+"F0.wireOp",EDGE,"E99"),sQuery(id+"F0.wireOp",EDGE,"E100"),sQuery(id+"F0.wireOp",EDGE,"E101"),sQuery(id+"F0.wireOp",EDGE,"E102"),sQuery(id+"F0.wireOp",EDGE,"E103"),sQuery(id+"F0.wireOp",EDGE,"E104"),sQuery(id+"F0.wireOp",EDGE,"E105"),sQuery(id+"F0.wireOp",EDGE,"E106"),sQuery(id+"F0.wireOp",EDGE,"E107"),sQuery(id+"F0.wireOp",EDGE,"E108"),sQuery(id+"F0.wireOp",EDGE,"E109"),sQuery(id+"F0.wireOp",EDGE,"E110"),sQuery(id+"F0.wireOp",EDGE,"E111"),sQuery(id+"F0.wireOp",EDGE,"E112"),sQuery(id+"F0.wireOp",EDGE,"E113"),sQuery(id+"F0.wireOp",EDGE,"E114"),sQuery(id+"F0.wireOp",EDGE,"E115"),sQuery(id+"F0.wireOp",EDGE,"E116"),sQuery(id+"F0.wireOp",EDGE,"E117"),sQuery(id+"F0.wireOp",EDGE,"E118"),sQuery(id+"F0.wireOp",EDGE,"E119"),sQuery(id+"F0.wireOp",EDGE,"E120"),sQuery(id+"F0.wireOp",EDGE,"E121"),sQuery(id+"F0.wireOp",EDGE,"E122"),sQuery(id+"F0.wireOp",EDGE,"E123"),sQuery(id+"F0.wireOp",EDGE,"E124"),sQuery(id+"F0.wireOp",EDGE,"E125"),sQuery(id+"F0.wireOp",EDGE,"E126"),sQuery(id+"F0.wireOp",EDGE,"E127"),sQuery(id+"F0.wireOp",EDGE,"E128"),sQuery(id+"F0.wireOp",EDGE,"E129"),sQuery(id+"F0.wireOp",EDGE,"E130"),sQuery(id+"F0.wireOp",EDGE,"E131"),sQuery(id+"F0.wireOp",EDGE,"E132"),sQuery(id+"F0.wireOp",EDGE,"E133"),sQuery(id+"F0.wireOp",EDGE,"E134"),sQuery(id+"F0.wireOp",EDGE,"E135"),sQuery(id+"F0.wireOp",EDGE,"E136"),sQuery(id+"F0.wireOp",EDGE,"E137"),sQuery(id+"F0.wireOp",EDGE,"E138"),sQuery(id+"F0.wireOp",EDGE,"E139"),sQuery(id+"F0.wireOp",EDGE,"E140"),sQuery(id+"F0.wireOp",EDGE,"E141"),sQuery(id+"F0.wireOp",EDGE,"E142"),sQuery(id+"F0.wireOp",EDGE,"E143"),sQuery(id+"F0.wireOp",EDGE,"E144"),sQuery(id+"F0.wireOp",EDGE,"E145"),sQuery(id+"F0.wireOp",EDGE,"E146"),sQuery(id+"F0.wireOp",EDGE,"E147"),sQuery(id+"F0.wireOp",EDGE,"E148"),sQuery(id+"F0.wireOp",EDGE,"E149"),sQuery(id+"F0.wireOp",EDGE,"E150"),sQuery(id+"F0.wireOp",EDGE,"E151"),sQuery(id+"F0.wireOp",EDGE,"E152"),sQuery(id+"F0.wireOp",EDGE,"E153"),sQuery(id+"F0.wireOp",EDGE,"E154"),sQuery(id+"F0.wireOp",EDGE,"E155"),sQuery(id+"F0.wireOp",EDGE,"E156"),sQuery(id+"F0.wireOp",EDGE,"E157"),sQuery(id+"F0.wireOp",EDGE,"E158"),sQuery(id+"F0.wireOp",EDGE,"E159"),sQuery(id+"F0.wireOp",EDGE,"E160"),sQuery(id+"F0.wireOp",EDGE,"E161"),sQuery(id+"F0.wireOp",EDGE,"E162"),sQuery(id+"F0.wireOp",EDGE,"E163"),sQuery(id+"F0.wireOp",EDGE,"E164"),sQuery(id+"F0.wireOp",EDGE,"E165"),sQuery(id+"F0.wireOp",EDGE,"E166"),sQuery(id+"F0.wireOp",EDGE,"E167"),sQuery(id+"F0.wireOp",EDGE,"E168"),sQuery(id+"F0.wireOp",EDGE,"E169"),sQuery(id+"F0.wireOp",EDGE,"E170"),sQuery(id+"F0.wireOp",EDGE,"E171"),sQuery(id+"F0.wireOp",EDGE,"E172"),sQuery(id+"F0.wireOp",EDGE,"E173"),sQuery(id+"F0.wireOp",EDGE,"E174"),sQuery(id+"F0.wireOp",EDGE,"E175"),sQuery(id+"F0.wireOp",EDGE,"E176"),sQuery(id+"F0.wireOp",EDGE,"E177"),sQuery(id+"F0.wireOp",EDGE,"E178"),sQuery(id+"F0.wireOp",EDGE,"E179"),sQuery(id+"F0.wireOp",EDGE,"E180"),sQuery(id+"F0.wireOp",EDGE,"E181"),sQuery(id+"F0.wireOp",EDGE,"E182"),sQuery(id+"F0.wireOp",EDGE,"E183"),sQuery(id+"F0.wireOp",EDGE,"E184"),sQuery(id+"F0.wireOp",EDGE,"E185"),sQuery(id+"F0.wireOp",EDGE,"E186"),sQuery(id+"F0.wireOp",EDGE,"E187"),sQuery(id+"F0.wireOp",EDGE,"E188"),sQuery(id+"F0.wireOp",EDGE,"E189"),sQuery(id+"F0.wireOp",EDGE,"E190"),sQuery(id+"F0.wireOp",EDGE,"E191"),sQuery(id+"F0.wireOp",EDGE,"E192"),sQuery(id+"F0.wireOp",EDGE,"E193"),sQuery(id+"F0.wireOp",EDGE,"E194"),sQuery(id+"F0.wireOp",EDGE,"E195"),sQuery(id+"F0.wireOp",EDGE,"E196"),sQuery(id+"F0.wireOp",EDGE,"E197"),sQuery(id+"F0.wireOp",EDGE,"E198"),sQuery(id+"F0.wireOp",EDGE,"E199"),sQuery(id+"F0.wireOp",EDGE,"E200"),sQuery(id+"F0.wireOp",EDGE,"E201"),sQuery(id+"F0.wireOp",EDGE,"E202"),sQuery(id+"F0.wireOp",EDGE,"E203"),sQuery(id+"F0.wireOp",EDGE,"E204"),sQuery(id+"F0.wireOp",EDGE,"E205"),sQuery(id+"F0.wireOp",EDGE,"E206"),sQuery(id+"F0.wireOp",EDGE,"E207"),sQuery(id+"F0.wireOp",EDGE,"E208"),sQuery(id+"F0.wireOp",EDGE,"E209"),sQuery(id+"F0.wireOp",EDGE,"E210"),sQuery(id+"F0.wireOp",EDGE,"E211"),sQuery(id+"F0.wireOp",EDGE,"E212"),sQuery(id+"F0.wireOp",EDGE,"E213"),sQuery(id+"F0.wireOp",EDGE,"E214"),sQuery(id+"F0.wireOp",EDGE,"E215"),sQuery(id+"F0.wireOp",EDGE,"E216"),sQuery(id+"F0.wireOp",EDGE,"E217"),sQuery(id+"F0.wireOp",EDGE,"E218"),sQuery(id+"F0.wireOp",EDGE,"E219"),sQuery(id+"F0.wireOp",EDGE,"E220"),sQuery(id+"F0.wireOp",EDGE,"E221"),sQuery(id+"F0.wireOp",EDGE,"E222"),sQuery(id+"F0.wireOp",EDGE,"E223"),sQuery(id+"F0.wireOp",EDGE,"E224"),sQuery(id+"F0.wireOp",EDGE,"E225"),sQuery(id+"F0.wireOp",EDGE,"E226"),sQuery(id+"F0.wireOp",EDGE,"E227"),sQuery(id+"F0.wireOp",EDGE,"E228"),sQuery(id+"F0.wireOp",EDGE,"E229"),sQuery(id+"F0.wireOp",EDGE,"E230"),sQuery(id+"F0.wireOp",EDGE,"E231"),sQuery(id+"F0.wireOp",EDGE,"E232"),sQuery(id+"F0.wireOp",EDGE,"E233"),sQuery(id+"F0.wireOp",EDGE,"E234"),sQuery(id+"F0.wireOp",EDGE,"E235"),sQuery(id+"F0.wireOp",EDGE,"E236"),sQuery(id+"F0.wireOp",EDGE,"E237"),sQuery(id+"F0.wireOp",EDGE,"E238"),sQuery(id+"F0.wireOp",EDGE,"E239"),sQuery(id+"F0.wireOp",EDGE,"E240"),sQuery(id+"F0.wireOp",EDGE,"E241"),sQuery(id+"F0.wireOp",EDGE,"E242"),sQuery(id+"F0.wireOp",EDGE,"E243"),sQuery(id+"F0.wireOp",EDGE,"E244"),sQuery(id+"F0.wireOp",EDGE,"E245"),sQuery(id+"F0.wireOp",EDGE,"E246"),sQuery(id+"F0.wireOp",EDGE,"E247"),sQuery(id+"F0.wireOp",EDGE,"E248"),sQuery(id+"F0.wireOp",EDGE,"E249"),sQuery(id+"F0.wireOp",EDGE,"E250"),sQuery(id+"F0.wireOp",EDGE,"E251"),sQuery(id+"F0.wireOp",EDGE,"E252"),sQuery(id+"F0.wireOp",EDGE,"E253"),sQuery(id+"F0.wireOp",EDGE,"E254"),sQuery(id+"F0.wireOp",EDGE,"E255"),sQuery(id+"F0.wireOp",EDGE,"E256"),sQuery(id+"F0.wireOp",EDGE,"E257"),sQuery(id+"F0.wireOp",EDGE,"E258"),sQuery(id+"F0.wireOp",EDGE,"E259"),sQuery(id+"F0.wireOp",EDGE,"E260"),sQuery(id+"F0.wireOp",EDGE,"E261")])]});
            transform(context, id + "F5", {"entities" : qUnion([Q0]), "transformType" : TransformType.TRANSLATION_3D, "dx" : 0 * mm, "dy" : -172 * mm, "dz" : 0 * mm, "makeCopy" : true});
        }
        {
            var Q0;
            Q0=makeQuery(id+"F5.opPattern","COPY",FACE,{"derivedFrom":makeQuery(id+"F1.opExtrude","CAP_FACE",FACE,{"disambiguationData":[OSD([sQuery(id+"F0.wireOp",EDGE,"E0"),sQuery(id+"F0.wireOp",EDGE,"E1"),sQuery(id+"F0.wireOp",EDGE,"E2"),sQuery(id+"F0.wireOp",EDGE,"E3"),sQuery(id+"F0.wireOp",EDGE,"E4"),sQuery(id+"F0.wireOp",EDGE,"E5"),sQuery(id+"F0.wireOp",EDGE,"E6"),sQuery(id+"F0.wireOp",EDGE,"E7"),sQuery(id+"F0.wireOp",EDGE,"E8"),sQuery(id+"F0.wireOp",EDGE,"E9"),sQuery(id+"F0.wireOp",EDGE,"E10"),sQuery(id+"F0.wireOp",EDGE,"E11"),sQuery(id+"F0.wireOp",EDGE,"E12"),sQuery(id+"F0.wireOp",EDGE,"E13"),sQuery(id+"F0.wireOp",EDGE,"E14"),sQuery(id+"F0.wireOp",EDGE,"E15"),sQuery(id+"F0.wireOp",EDGE,"E16"),sQuery(id+"F0.wireOp",EDGE,"E17"),sQuery(id+"F0.wireOp",EDGE,"E18"),sQuery(id+"F0.wireOp",EDGE,"E19"),sQuery(id+"F0.wireOp",EDGE,"E20"),sQuery(id+"F0.wireOp",EDGE,"E21"),sQuery(id+"F0.wireOp",EDGE,"E22"),sQuery(id+"F0.wireOp",EDGE,"E23"),sQuery(id+"F0.wireOp",EDGE,"E24"),sQuery(id+"F0.wireOp",EDGE,"E25"),sQuery(id+"F0.wireOp",EDGE,"E26"),sQuery(id+"F0.wireOp",EDGE,"E27"),sQuery(id+"F0.wireOp",EDGE,"E28"),sQuery(id+"F0.wireOp",EDGE,"E29"),sQuery(id+"F0.wireOp",EDGE,"E30"),sQuery(id+"F0.wireOp",EDGE,"E31"),sQuery(id+"F0.wireOp",EDGE,"E32"),sQuery(id+"F0.wireOp",EDGE,"E33"),sQuery(id+"F0.wireOp",EDGE,"E34"),sQuery(id+"F0.wireOp",EDGE,"E35"),sQuery(id+"F0.wireOp",EDGE,"E36"),sQuery(id+"F0.wireOp",EDGE,"E37"),sQuery(id+"F0.wireOp",EDGE,"E38"),sQuery(id+"F0.wireOp",EDGE,"E39"),sQuery(id+"F0.wireOp",EDGE,"E40"),sQuery(id+"F0.wireOp",EDGE,"E41"),sQuery(id+"F0.wireOp",EDGE,"E42"),sQuery(id+"F0.wireOp",EDGE,"E43"),sQuery(id+"F0.wireOp",EDGE,"E44"),sQuery(id+"F0.wireOp",EDGE,"E45"),sQuery(id+"F0.wireOp",EDGE,"E46"),sQuery(id+"F0.wireOp",EDGE,"E47"),sQuery(id+"F0.wireOp",EDGE,"E48"),sQuery(id+"F0.wireOp",EDGE,"E49"),sQuery(id+"F0.wireOp",EDGE,"E50"),sQuery(id+"F0.wireOp",EDGE,"E51"),sQuery(id+"F0.wireOp",EDGE,"E52"),sQuery(id+"F0.wireOp",EDGE,"E53"),sQuery(id+"F0.wireOp",EDGE,"E54"),sQuery(id+"F0.wireOp",EDGE,"E55"),sQuery(id+"F0.wireOp",EDGE,"E56"),sQuery(id+"F0.wireOp",EDGE,"E57"),sQuery(id+"F0.wireOp",EDGE,"E58"),sQuery(id+"F0.wireOp",EDGE,"E59"),sQuery(id+"F0.wireOp",EDGE,"E60"),sQuery(id+"F0.wireOp",EDGE,"E61"),sQuery(id+"F0.wireOp",EDGE,"E62"),sQuery(id+"F0.wireOp",EDGE,"E63"),sQuery(id+"F0.wireOp",EDGE,"E64"),sQuery(id+"F0.wireOp",EDGE,"E65"),sQuery(id+"F0.wireOp",EDGE,"E66"),sQuery(id+"F0.wireOp",EDGE,"E67"),sQuery(id+"F0.wireOp",EDGE,"E68"),sQuery(id+"F0.wireOp",EDGE,"E69"),sQuery(id+"F0.wireOp",EDGE,"E70"),sQuery(id+"F0.wireOp",EDGE,"E71"),sQuery(id+"F0.wireOp",EDGE,"E72"),sQuery(id+"F0.wireOp",EDGE,"E73"),sQuery(id+"F0.wireOp",EDGE,"E74"),sQuery(id+"F0.wireOp",EDGE,"E75"),sQuery(id+"F0.wireOp",EDGE,"E76"),sQuery(id+"F0.wireOp",EDGE,"E77"),sQuery(id+"F0.wireOp",EDGE,"E78"),sQuery(id+"F0.wireOp",EDGE,"E79"),sQuery(id+"F0.wireOp",EDGE,"E80"),sQuery(id+"F0.wireOp",EDGE,"E81"),sQuery(id+"F0.wireOp",EDGE,"E82"),sQuery(id+"F0.wireOp",EDGE,"E83"),sQuery(id+"F0.wireOp",EDGE,"E84"),sQuery(id+"F0.wireOp",EDGE,"E85"),sQuery(id+"F0.wireOp",EDGE,"E86"),sQuery(id+"F0.wireOp",EDGE,"E87"),sQuery(id+"F0.wireOp",EDGE,"E88"),sQuery(id+"F0.wireOp",EDGE,"E89"),sQuery(id+"F0.wireOp",EDGE,"E90"),sQuery(id+"F0.wireOp",EDGE,"E91"),sQuery(id+"F0.wireOp",EDGE,"E92"),sQuery(id+"F0.wireOp",EDGE,"E93"),sQuery(id+"F0.wireOp",EDGE,"E94"),sQuery(id+"F0.wireOp",EDGE,"E95"),sQuery(id+"F0.wireOp",EDGE,"E96"),sQuery(id+"F0.wireOp",EDGE,"E97"),sQuery(id+"F0.wireOp",EDGE,"E98"),sQuery(id+"F0.wireOp",EDGE,"E99"),sQuery(id+"F0.wireOp",EDGE,"E100"),sQuery(id+"F0.wireOp",EDGE,"E101"),sQuery(id+"F0.wireOp",EDGE,"E102"),sQuery(id+"F0.wireOp",EDGE,"E103"),sQuery(id+"F0.wireOp",EDGE,"E104"),sQuery(id+"F0.wireOp",EDGE,"E105"),sQuery(id+"F0.wireOp",EDGE,"E106"),sQuery(id+"F0.wireOp",EDGE,"E107"),sQuery(id+"F0.wireOp",EDGE,"E108"),sQuery(id+"F0.wireOp",EDGE,"E109"),sQuery(id+"F0.wireOp",EDGE,"E110"),sQuery(id+"F0.wireOp",EDGE,"E111"),sQuery(id+"F0.wireOp",EDGE,"E112"),sQuery(id+"F0.wireOp",EDGE,"E113"),sQuery(id+"F0.wireOp",EDGE,"E114"),sQuery(id+"F0.wireOp",EDGE,"E115"),sQuery(id+"F0.wireOp",EDGE,"E116"),sQuery(id+"F0.wireOp",EDGE,"E117"),sQuery(id+"F0.wireOp",EDGE,"E118"),sQuery(id+"F0.wireOp",EDGE,"E119"),sQuery(id+"F0.wireOp",EDGE,"E120"),sQuery(id+"F0.wireOp",EDGE,"E121"),sQuery(id+"F0.wireOp",EDGE,"E122"),sQuery(id+"F0.wireOp",EDGE,"E123"),sQuery(id+"F0.wireOp",EDGE,"E124"),sQuery(id+"F0.wireOp",EDGE,"E125"),sQuery(id+"F0.wireOp",EDGE,"E126"),sQuery(id+"F0.wireOp",EDGE,"E127"),sQuery(id+"F0.wireOp",EDGE,"E128"),sQuery(id+"F0.wireOp",EDGE,"E129"),sQuery(id+"F0.wireOp",EDGE,"E130"),sQuery(id+"F0.wireOp",EDGE,"E131"),sQuery(id+"F0.wireOp",EDGE,"E132"),sQuery(id+"F0.wireOp",EDGE,"E133"),sQuery(id+"F0.wireOp",EDGE,"E134"),sQuery(id+"F0.wireOp",EDGE,"E135"),sQuery(id+"F0.wireOp",EDGE,"E136"),sQuery(id+"F0.wireOp",EDGE,"E137"),sQuery(id+"F0.wireOp",EDGE,"E138"),sQuery(id+"F0.wireOp",EDGE,"E139"),sQuery(id+"F0.wireOp",EDGE,"E140"),sQuery(id+"F0.wireOp",EDGE,"E141"),sQuery(id+"F0.wireOp",EDGE,"E142"),sQuery(id+"F0.wireOp",EDGE,"E143"),sQuery(id+"F0.wireOp",EDGE,"E144"),sQuery(id+"F0.wireOp",EDGE,"E145"),sQuery(id+"F0.wireOp",EDGE,"E146"),sQuery(id+"F0.wireOp",EDGE,"E147"),sQuery(id+"F0.wireOp",EDGE,"E148"),sQuery(id+"F0.wireOp",EDGE,"E149"),sQuery(id+"F0.wireOp",EDGE,"E150"),sQuery(id+"F0.wireOp",EDGE,"E151"),sQuery(id+"F0.wireOp",EDGE,"E152"),sQuery(id+"F0.wireOp",EDGE,"E153"),sQuery(id+"F0.wireOp",EDGE,"E154"),sQuery(id+"F0.wireOp",EDGE,"E155"),sQuery(id+"F0.wireOp",EDGE,"E156"),sQuery(id+"F0.wireOp",EDGE,"E157"),sQuery(id+"F0.wireOp",EDGE,"E158"),sQuery(id+"F0.wireOp",EDGE,"E159"),sQuery(id+"F0.wireOp",EDGE,"E160"),sQuery(id+"F0.wireOp",EDGE,"E161"),sQuery(id+"F0.wireOp",EDGE,"E162"),sQuery(id+"F0.wireOp",EDGE,"E163"),sQuery(id+"F0.wireOp",EDGE,"E164"),sQuery(id+"F0.wireOp",EDGE,"E165"),sQuery(id+"F0.wireOp",EDGE,"E166"),sQuery(id+"F0.wireOp",EDGE,"E167"),sQuery(id+"F0.wireOp",EDGE,"E168"),sQuery(id+"F0.wireOp",EDGE,"E169"),sQuery(id+"F0.wireOp",EDGE,"E170"),sQuery(id+"F0.wireOp",EDGE,"E171"),sQuery(id+"F0.wireOp",EDGE,"E172"),sQuery(id+"F0.wireOp",EDGE,"E173"),sQuery(id+"F0.wireOp",EDGE,"E174"),sQuery(id+"F0.wireOp",EDGE,"E175"),sQuery(id+"F0.wireOp",EDGE,"E176"),sQuery(id+"F0.wireOp",EDGE,"E177"),sQuery(id+"F0.wireOp",EDGE,"E178"),sQuery(id+"F0.wireOp",EDGE,"E179"),sQuery(id+"F0.wireOp",EDGE,"E180"),sQuery(id+"F0.wireOp",EDGE,"E181"),sQuery(id+"F0.wireOp",EDGE,"E182"),sQuery(id+"F0.wireOp",EDGE,"E183"),sQuery(id+"F0.wireOp",EDGE,"E184"),sQuery(id+"F0.wireOp",EDGE,"E185"),sQuery(id+"F0.wireOp",EDGE,"E186"),sQuery(id+"F0.wireOp",EDGE,"E187"),sQuery(id+"F0.wireOp",EDGE,"E188"),sQuery(id+"F0.wireOp",EDGE,"E189"),sQuery(id+"F0.wireOp",EDGE,"E190"),sQuery(id+"F0.wireOp",EDGE,"E191"),sQuery(id+"F0.wireOp",EDGE,"E192"),sQuery(id+"F0.wireOp",EDGE,"E193"),sQuery(id+"F0.wireOp",EDGE,"E194"),sQuery(id+"F0.wireOp",EDGE,"E195"),sQuery(id+"F0.wireOp",EDGE,"E196"),sQuery(id+"F0.wireOp",EDGE,"E197"),sQuery(id+"F0.wireOp",EDGE,"E198"),sQuery(id+"F0.wireOp",EDGE,"E199"),sQuery(id+"F0.wireOp",EDGE,"E200"),sQuery(id+"F0.wireOp",EDGE,"E201"),sQuery(id+"F0.wireOp",EDGE,"E202"),sQuery(id+"F0.wireOp",EDGE,"E203"),sQuery(id+"F0.wireOp",EDGE,"E204"),sQuery(id+"F0.wireOp",EDGE,"E205"),sQuery(id+"F0.wireOp",EDGE,"E206"),sQuery(id+"F0.wireOp",EDGE,"E207"),sQuery(id+"F0.wireOp",EDGE,"E208"),sQuery(id+"F0.wireOp",EDGE,"E209"),sQuery(id+"F0.wireOp",EDGE,"E210"),sQuery(id+"F0.wireOp",EDGE,"E211"),sQuery(id+"F0.wireOp",EDGE,"E212"),sQuery(id+"F0.wireOp",EDGE,"E213"),sQuery(id+"F0.wireOp",EDGE,"E214"),sQuery(id+"F0.wireOp",EDGE,"E215"),sQuery(id+"F0.wireOp",EDGE,"E216"),sQuery(id+"F0.wireOp",EDGE,"E217"),sQuery(id+"F0.wireOp",EDGE,"E218"),sQuery(id+"F0.wireOp",EDGE,"E219"),sQuery(id+"F0.wireOp",EDGE,"E220"),sQuery(id+"F0.wireOp",EDGE,"E221"),sQuery(id+"F0.wireOp",EDGE,"E222"),sQuery(id+"F0.wireOp",EDGE,"E223"),sQuery(id+"F0.wireOp",EDGE,"E224"),sQuery(id+"F0.wireOp",EDGE,"E225"),sQuery(id+"F0.wireOp",EDGE,"E226"),sQuery(id+"F0.wireOp",EDGE,"E227"),sQuery(id+"F0.wireOp",EDGE,"E228"),sQuery(id+"F0.wireOp",EDGE,"E229"),sQuery(id+"F0.wireOp",EDGE,"E230"),sQuery(id+"F0.wireOp",EDGE,"E231"),sQuery(id+"F0.wireOp",EDGE,"E232"),sQuery(id+"F0.wireOp",EDGE,"E233"),sQuery(id+"F0.wireOp",EDGE,"E234"),sQuery(id+"F0.wireOp",EDGE,"E235"),sQuery(id+"F0.wireOp",EDGE,"E236"),sQuery(id+"F0.wireOp",EDGE,"E237"),sQuery(id+"F0.wireOp",EDGE,"E238"),sQuery(id+"F0.wireOp",EDGE,"E239"),sQuery(id+"F0.wireOp",EDGE,"E240"),sQuery(id+"F0.wireOp",EDGE,"E241"),sQuery(id+"F0.wireOp",EDGE,"E242"),sQuery(id+"F0.wireOp",EDGE,"E243"),sQuery(id+"F0.wireOp",EDGE,"E244"),sQuery(id+"F0.wireOp",EDGE,"E245"),sQuery(id+"F0.wireOp",EDGE,"E246"),sQuery(id+"F0.wireOp",EDGE,"E247"),sQuery(id+"F0.wireOp",EDGE,"E248"),sQuery(id+"F0.wireOp",EDGE,"E249"),sQuery(id+"F0.wireOp",EDGE,"E250"),sQuery(id+"F0.wireOp",EDGE,"E251"),sQuery(id+"F0.wireOp",EDGE,"E252"),sQuery(id+"F0.wireOp",EDGE,"E253"),sQuery(id+"F0.wireOp",EDGE,"E254"),sQuery(id+"F0.wireOp",EDGE,"E255"),sQuery(id+"F0.wireOp",EDGE,"E256"),sQuery(id+"F0.wireOp",EDGE,"E257"),sQuery(id+"F0.wireOp",EDGE,"E258"),sQuery(id+"F0.wireOp",EDGE,"E259"),sQuery(id+"F0.wireOp",EDGE,"E260"),sQuery(id+"F0.wireOp",EDGE,"E261")])],"isStart":false}),"instanceName":"1"});
            var sketch = newSketch(context, id + "F6", { "sketchPlane" : qUnion([Q0])});
            skLineSegment(sketch, "E275.bottom", {"start": v(-28.07, -132.15) * mm, "end": v(28.07, -132.15) * mm});
            skLineSegment(sketch, "E275.top", {"start": v(-28.07, -194.15) * mm, "end": v(28.07, -194.15) * mm});
            skLineSegment(sketch, "E275.left", {"start": v(-28.07, -132.15) * mm, "end": v(-28.07, -194.15) * mm});
            skLineSegment(sketch, "E275.right", {"start": v(28.07, -132.15) * mm, "end": v(28.07, -194.15) * mm});
            skSolve(sketch);
        }
        {
            var Q0;
            Q0=makeQuery(id+"F6.imprint","IMPRINT",FACE,{"disambiguationData":[TD([[makeQuery(id+"F6.imprint","IMPRINT",EDGE,{"derivedFrom":makeQuery(id+"F5.opPattern","COPY",EDGE,{"derivedFrom":makeQuery(id+"F1.opExtrude","CAP_EDGE",EDGE,{"disambiguationData":[OSD([sQuery(id+"F0.wireOp",EDGE,"E1")])],"isStart":false}),"instanceName":"1"})}),1.0]])]});
            extrude(context, id + "F7", {"entities" : qUnion([Q0]), "operationType" : NewBodyOperationType.REMOVE, "oppositeDirection" : true, "depth" : 25 * mm, "offsetDistance" : 25 * mm});
        }
        {
            var Q0;
            Q0=makeQuery(id+"F1.opExtrude","CAP_EDGE",EDGE,{"disambiguationData":[OSD([sQuery(id+"F0.wireOp",EDGE,"E150")])],"isStart":true});
            cPoint(context, id + "F8", {"entities" : qUnion([Q0]), "parameter" : 0.5});
        }
        {
            var Q0;
            Q0=qCreatedBy(id+"F8",VERTEX);
            var Q1;
            Q1=makeQuery(id+"F1.opExtrude","CAP_EDGE",EDGE,{"disambiguationData":[OSD([sQuery(id+"F0.wireOp",EDGE,"E150")])],"isStart":true});
            cPlane(context, id + "F9", {"entities" : qUnion([Q0, Q1]), "cplaneType" : CPlaneType.LINE_POINT, "offset" : 25 * mm, "width" : 150 * mm, "height" : 150 * mm});
        }
        {
            var Q0;
            Q0=qCreatedBy(id+"F9.planeOp",FACE);
            var sketch = newSketch(context, id + "F10", { "sketchPlane" : qUnion([Q0])});
            skCircle(sketch, "E276", {"center": v(-85, -6) * mm, "radius": 7.5 * mm, "construction": true});
            skCircle(sketch, "E277", {"center": v(85, -6) * mm, "radius": 7.5 * mm, "construction": true});
            skSolve(sketch);
        }
        {
            var Q0;
            Q0=makeQuery(id+"F1.opExtrude","CAP_EDGE",EDGE,{"disambiguationData":[OSD([sQuery(id+"F0.wireOp",EDGE,"E134")])],"isStart":true});
            cPoint(context, id + "F11", {"entities" : qUnion([Q0]), "parameter" : 0.5});
        }
        {
            var Q0;
            Q0=qCreatedBy(id+"F11",VERTEX);
            var Q1;
            Q1=makeQuery(id+"F1.opExtrude","CAP_EDGE",EDGE,{"disambiguationData":[OSD([sQuery(id+"F0.wireOp",EDGE,"E134")])],"isStart":true});
            cPlane(context, id + "F12", {"entities" : qUnion([Q0, Q1]), "cplaneType" : CPlaneType.LINE_POINT, "offset" : 25 * mm, "width" : 150 * mm, "height" : 150 * mm});
        }
        {
            var Q0;
            Q0=qCreatedBy(id+"F12.planeOp",FACE);
            var sketch = newSketch(context, id + "F13", { "sketchPlane" : qUnion([Q0])});
            skCircle(sketch, "E278", {"center": v(-85, -6) * mm, "radius": 7.5 * mm, "construction": true});
            skCircle(sketch, "E279", {"center": v(85, -6) * mm, "radius": 7.5 * mm, "construction": true});
            skSolve(sketch);
        }
    });
